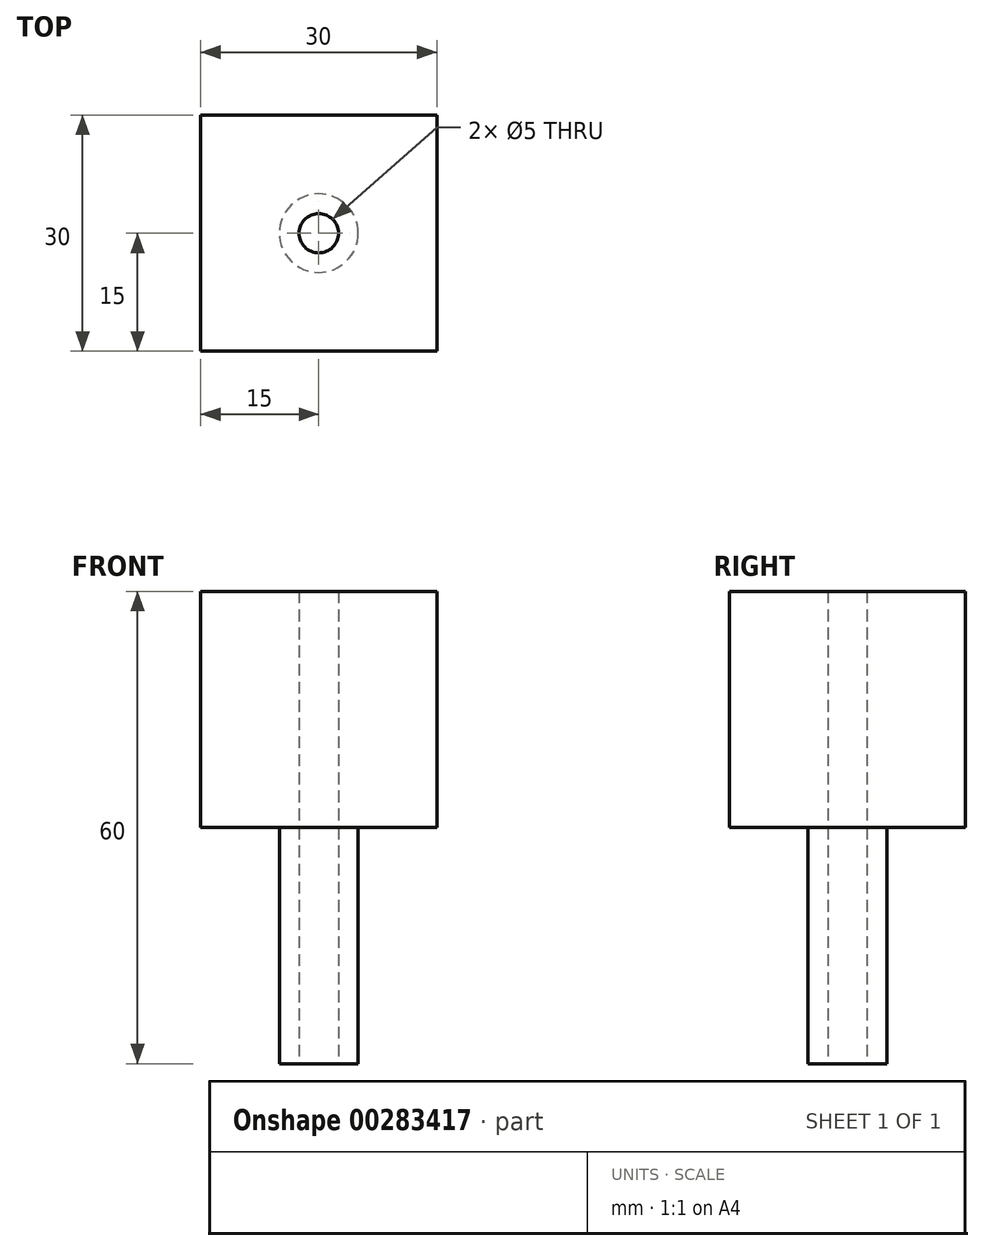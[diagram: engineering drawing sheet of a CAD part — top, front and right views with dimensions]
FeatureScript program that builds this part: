
annotation { "Feature Type Name" : "Feature", "Feature Type Description" : "" }
export const myFeature = defineFeature(function(context is Context, id is Id, definition is map)
    precondition{}
    {
        {
            var Q0;
            Q0=qCreatedBy(makeId("Top.planeOp"),FACE);
            var sketch = newSketch(context, id + "F0", { "sketchPlane" : qUnion([Q0])});
            skLineSegment(sketch, "E0.bottom", {"start": v(15, 15) * mm, "end": v(-15, 15) * mm});
            skLineSegment(sketch, "E0.top", {"start": v(15, -15) * mm, "end": v(-15, -15) * mm});
            skLineSegment(sketch, "E0.left", {"start": v(15, 15) * mm, "end": v(15, -15) * mm});
            skLineSegment(sketch, "E0.right", {"start": v(-15, 15) * mm, "end": v(-15, -15) * mm});
            skPoint(sketch, "E0.middle", {"position": v(0, 0) * mm});
            skSolve(sketch);
        }
        {
            var Q0;
            Q0 = qSketchRegion(id + "F0", true);
            extrude(context, id + "F1", {"entities" : qUnion([Q0]), "depth" : 30 * mm});
        }
        {
            var Q0;
            Q0=qCreatedBy(makeId("Top.planeOp"),FACE);
            var sketch = newSketch(context, id + "F2", { "sketchPlane" : qUnion([Q0])});
            skCircle(sketch, "E1", {"center": v(0, 0) * mm, "radius": 5 * mm});
            skSolve(sketch);
        }
        {
            var Q0;
            Q0=makeQuery(id+"F2.imprint","IMPRINT",FACE,{"disambiguationData":[TD([[makeQuery(id+"F2.imprint","IMPRINT",EDGE,{"derivedFrom":sQuery(id+"F2.wireOp",EDGE,"E1")}),1.0]])]});
            var Q1;
            Q1=sQuery(id+"F2.wireOp",EDGE,"E1");
            extrude(context, id + "F3", {"entities" : qUnion([Q0]), "surfaceEntities" : qUnion([Q1]), "oppositeDirection" : true, "depth" : 30 * mm});
        }
        {
            var Q0;
            Q0=makeQuery(id+"F3.opExtrude","CAP_FACE",FACE,{"disambiguationData":[OSD([sQuery(id+"F2.wireOp",EDGE,"E1")])],"isStart":false});
            var sketch = newSketch(context, id + "F4", { "sketchPlane" : qUnion([Q0])});
            skCircle(sketch, "E2", {"center": v(0, 0) * mm, "radius": 2.5 * mm});
            skSolve(sketch);
        }
        {
            var Q0;
            Q0 = qSketchRegion(id + "F4", true);
            extrude(context, id + "F5", {"entities" : qUnion([Q0]), "operationType" : NewBodyOperationType.REMOVE, "oppositeDirection" : true, "depth" : 70 * mm});
        }
    });
